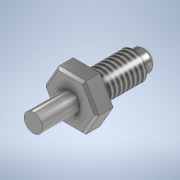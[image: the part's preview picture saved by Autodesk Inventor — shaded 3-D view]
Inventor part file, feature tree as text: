
AUTODESK INVENTOR PART (.ipt)
format: ipt  version: 2020 (Build 240168000, 168)  size: 151,552 bytes
history: native  units: mm
features: sketch x3, extrude x2, revolve x1, thread x1, chamfer x1
ambient origin geometry x8: Origin, YZ Plane, XZ Plane, XY Plane, X Axis, Y Axis, Z Axis, Center Point
bodies: Body1 (feature_tree)
feature tree (8):
  revolve  "Revolution1"  [1 undecoded]
  thread  "Thread1"  [1 undecoded]
  extrude  "Extrusion2"  Depth=2.0mm
  chamfer  "Chamfer1"  Distance=3.0mm
  extrude  "Extrusion3"  TaperAngle=90.0deg  [1 undecoded]
  sketch  "Sketch2"  dims[d3=1.0mm d4=1.0mm d5=1.25mm]
  sketch  "Sketch3"  dims[d6=2.0mm d7=0.75mm]
  sketch  "Sketch4"  dims[d8=10.0mm d9=3.0mm d10=90.0deg d11=10.0mm d12=0.0mm d13=10.0mm d14=3.5mm d15=0.0mm d16=0.5mm d17=0.5mm d18=45.0deg d19=4.0mm d20=8.0mm d21=0.0mm]
note: 3 required parameter values undecoded (feature->parameter linkage not recoverable at this tier; creation-order binding heuristic only, values carry confidence <= 0.55)